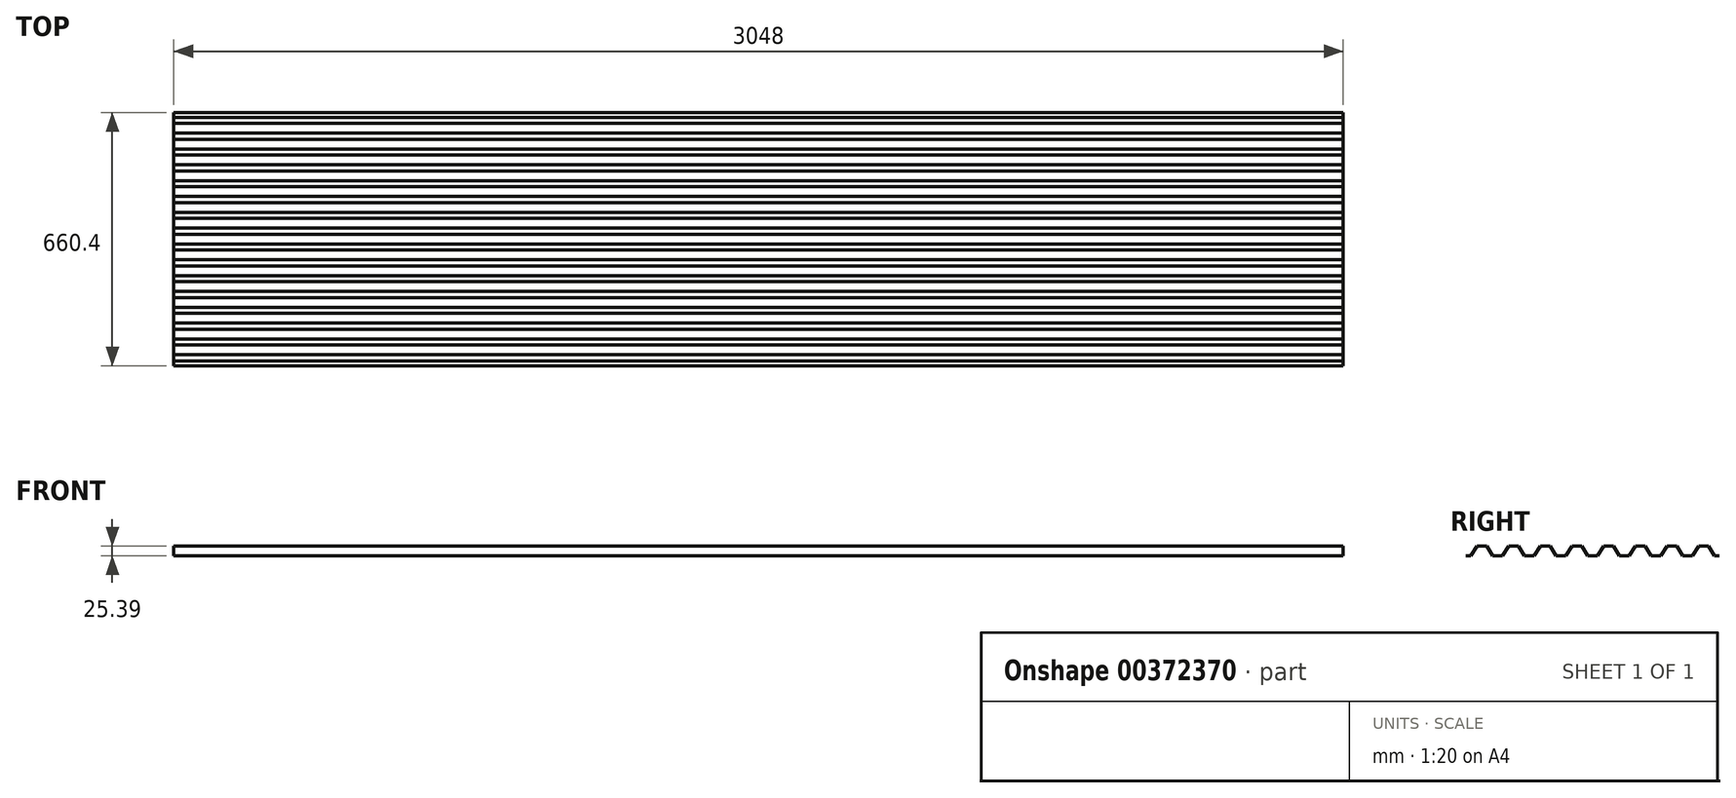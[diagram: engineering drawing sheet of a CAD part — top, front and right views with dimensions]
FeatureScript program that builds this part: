
annotation { "Feature Type Name" : "Feature", "Feature Type Description" : "" }
export const myFeature = defineFeature(function(context is Context, id is Id, definition is map)
    precondition{}
    {
        {
            var Q0;
            Q0=qCreatedBy(makeId("Right.planeOp"),FACE);
            var sketch = newSketch(context, id + "F0", { "sketchPlane" : qUnion([Q0])});
            skLineSegment(sketch, "E0", {"start": v(-328.87, 0) * mm, "end": v(-316.17, 0) * mm});
            skLineSegment(sketch, "E1", {"start": v(-316.17, 0) * mm, "end": v(-300.3, 25.4) * mm});
            skLineSegment(sketch, "E2", {"start": v(-300.3, 25.4) * mm, "end": v(-274.9, 25.4) * mm});
            skLineSegment(sketch, "E3", {"start": v(-274.9, 25.4) * mm, "end": v(-259.02, 0) * mm});
            skLineSegment(sketch, "E4", {"start": v(-259.02, 0) * mm, "end": v(-246.32, 0) * mm});
            skLineSegment(sketch, "E5.1.0.0", {"start": v(-233.62, 0) * mm, "end": v(-217.75, 25.4) * mm});
            skLineSegment(sketch, "E5.1.0.1", {"start": v(-192.35, 25.4) * mm, "end": v(-176.47, 0) * mm});
            skLineSegment(sketch, "E5.1.0.2", {"start": v(-217.75, 25.4) * mm, "end": v(-192.35, 25.4) * mm});
            skLineSegment(sketch, "E5.1.0.3", {"start": v(-246.32, 0) * mm, "end": v(-233.62, 0) * mm});
            skLineSegment(sketch, "E5.1.0.4", {"start": v(-176.47, 0) * mm, "end": v(-163.77, 0) * mm});
            skLineSegment(sketch, "E5.2.0.0", {"start": v(-151.07, 0) * mm, "end": v(-135.2, 25.4) * mm});
            skLineSegment(sketch, "E5.2.0.1", {"start": v(-109.8, 25.4) * mm, "end": v(-93.92, 0) * mm});
            skLineSegment(sketch, "E5.2.0.2", {"start": v(-135.2, 25.4) * mm, "end": v(-109.8, 25.4) * mm});
            skLineSegment(sketch, "E5.2.0.3", {"start": v(-163.77, 0) * mm, "end": v(-151.07, 0) * mm});
            skLineSegment(sketch, "E5.2.0.4", {"start": v(-93.92, 0) * mm, "end": v(-81.22, 0) * mm});
            skLineSegment(sketch, "E5.direction1", {"start": v(-328.87, 0) * mm, "end": v(-246.32, 0) * mm, "construction": true});
            skLineSegment(sketch, "E6.0.3.0", {"start": v(-68.52, 0) * mm, "end": v(-52.65, 25.4) * mm});
            skLineSegment(sketch, "E6.3.3.0", {"start": v(-27.25, 25.4) * mm, "end": v(-11.37, 0) * mm});
            skLineSegment(sketch, "E6.6.3.0", {"start": v(-52.65, 25.4) * mm, "end": v(-27.25, 25.4) * mm});
            skLineSegment(sketch, "E6.9.3.0", {"start": v(-81.22, 0) * mm, "end": v(-68.52, 0) * mm});
            skLineSegment(sketch, "E6.12.3.0", {"start": v(-11.37, 0) * mm, "end": v(1.33, 0) * mm});
            skLineSegment(sketch, "E6.0.4.0", {"start": v(14.03, 0) * mm, "end": v(29.9, 25.4) * mm});
            skLineSegment(sketch, "E6.3.4.0", {"start": v(55.3, 25.4) * mm, "end": v(71.18, 0) * mm});
            skLineSegment(sketch, "E6.6.4.0", {"start": v(29.9, 25.4) * mm, "end": v(55.3, 25.4) * mm});
            skLineSegment(sketch, "E6.9.4.0", {"start": v(1.33, 0) * mm, "end": v(14.03, 0) * mm});
            skLineSegment(sketch, "E6.12.4.0", {"start": v(71.18, 0) * mm, "end": v(83.88, 0) * mm});
            skLineSegment(sketch, "E6.0.5.0", {"start": v(96.58, 0) * mm, "end": v(112.45, 25.4) * mm});
            skLineSegment(sketch, "E6.3.5.0", {"start": v(137.85, 25.4) * mm, "end": v(153.73, 0) * mm});
            skLineSegment(sketch, "E6.6.5.0", {"start": v(112.45, 25.4) * mm, "end": v(137.85, 25.4) * mm});
            skLineSegment(sketch, "E6.9.5.0", {"start": v(83.88, 0) * mm, "end": v(96.58, 0) * mm});
            skLineSegment(sketch, "E6.12.5.0", {"start": v(153.73, 0) * mm, "end": v(166.43, 0) * mm});
            skLineSegment(sketch, "E6.0.6.0", {"start": v(179.13, 0) * mm, "end": v(195, 25.4) * mm});
            skLineSegment(sketch, "E6.3.6.0", {"start": v(220.4, 25.4) * mm, "end": v(236.28, 0) * mm});
            skLineSegment(sketch, "E6.6.6.0", {"start": v(195, 25.4) * mm, "end": v(220.4, 25.4) * mm});
            skLineSegment(sketch, "E6.9.6.0", {"start": v(166.43, 0) * mm, "end": v(179.13, 0) * mm});
            skLineSegment(sketch, "E6.12.6.0", {"start": v(236.28, 0) * mm, "end": v(248.98, 0) * mm});
            skLineSegment(sketch, "E6.0.7.0", {"start": v(261.68, 0) * mm, "end": v(277.55, 25.4) * mm});
            skLineSegment(sketch, "E6.3.7.0", {"start": v(302.95, 25.4) * mm, "end": v(318.83, 0) * mm});
            skLineSegment(sketch, "E6.6.7.0", {"start": v(277.55, 25.4) * mm, "end": v(302.95, 25.4) * mm});
            skLineSegment(sketch, "E6.9.7.0", {"start": v(248.98, 0) * mm, "end": v(261.68, 0) * mm});
            skLineSegment(sketch, "E6.12.7.0", {"start": v(318.83, 0) * mm, "end": v(331.53, 0) * mm});
            skSolve(sketch);
        }
        {
            var Q0;
            Q0=sQuery(id+"F0.wireOp",EDGE,"E6.0.6.0");
            var Q1;
            Q1=sQuery(id+"F0.wireOp",EDGE,"E5.1.0.1");
            var Q2;
            Q2=sQuery(id+"F0.wireOp",EDGE,"E6.6.4.0");
            var Q3;
            Q3=sQuery(id+"F0.wireOp",EDGE,"E6.3.3.0");
            var Q4;
            Q4=sQuery(id+"F0.wireOp",EDGE,"E6.3.5.0");
            var Q5;
            Q5=sQuery(id+"F0.wireOp",EDGE,"E6.3.7.0");
            var Q6;
            Q6=sQuery(id+"F0.wireOp",EDGE,"E3");
            var Q7;
            Q7=sQuery(id+"F0.wireOp",EDGE,"E6.0.7.0");
            var Q8;
            Q8=sQuery(id+"F0.wireOp",EDGE,"E6.6.7.0");
            var Q9;
            Q9=sQuery(id+"F0.wireOp",EDGE,"E5.2.0.0");
            var Q10;
            Q10=sQuery(id+"F0.wireOp",EDGE,"E6.3.4.0");
            var Q11;
            Q11=sQuery(id+"F0.wireOp",EDGE,"E5.1.0.0");
            var Q12;
            Q12=sQuery(id+"F0.wireOp",EDGE,"E6.6.3.0");
            var Q13;
            Q13=sQuery(id+"F0.wireOp",EDGE,"E1");
            var Q14;
            Q14=sQuery(id+"F0.wireOp",EDGE,"E2");
            var Q15;
            Q15=sQuery(id+"F0.wireOp",EDGE,"E6.0.3.0");
            var Q16;
            Q16=sQuery(id+"F0.wireOp",EDGE,"E5.1.0.2");
            var Q17;
            Q17=sQuery(id+"F0.wireOp",EDGE,"E6.6.6.0");
            var Q18;
            Q18=sQuery(id+"F0.wireOp",EDGE,"E6.0.5.0");
            var Q19;
            Q19=sQuery(id+"F0.wireOp",EDGE,"E6.3.6.0");
            var Q20;
            Q20=sQuery(id+"F0.wireOp",EDGE,"E6.6.5.0");
            var Q21;
            Q21=sQuery(id+"F0.wireOp",EDGE,"E5.2.0.2");
            var Q22;
            Q22=sQuery(id+"F0.wireOp",EDGE,"E6.0.4.0");
            var Q23;
            Q23=sQuery(id+"F0.wireOp",EDGE,"E5.2.0.1");
            var Q24;
            Q24=sQuery(id+"F0.wireOp",EDGE,"E6.12.7.0");
            var Q25;
            Q25=sQuery(id+"F0.wireOp",EDGE,"E6.12.4.0");
            var Q26;
            Q26=sQuery(id+"F0.wireOp",EDGE,"E4");
            var Q27;
            Q27=sQuery(id+"F0.wireOp",EDGE,"E6.12.3.0");
            var Q28;
            Q28=sQuery(id+"F0.wireOp",EDGE,"E6.9.3.0");
            var Q29;
            Q29=sQuery(id+"F0.wireOp",EDGE,"E5.2.0.3");
            var Q30;
            Q30=sQuery(id+"F0.wireOp",EDGE,"E6.9.4.0");
            var Q31;
            Q31=sQuery(id+"F0.wireOp",EDGE,"E5.2.0.4");
            var Q32;
            Q32=sQuery(id+"F0.wireOp",EDGE,"E6.9.5.0");
            var Q33;
            Q33=sQuery(id+"F0.wireOp",EDGE,"E6.9.7.0");
            var Q34;
            Q34=sQuery(id+"F0.wireOp",EDGE,"E6.12.6.0");
            var Q35;
            Q35=sQuery(id+"F0.wireOp",EDGE,"E6.12.5.0");
            var Q36;
            Q36=sQuery(id+"F0.wireOp",EDGE,"E5.1.0.4");
            var Q37;
            Q37=sQuery(id+"F0.wireOp",EDGE,"E5.1.0.3");
            var Q38;
            Q38=sQuery(id+"F0.wireOp",EDGE,"E0");
            var Q39;
            Q39=sQuery(id+"F0.wireOp",EDGE,"E6.9.6.0");
            extrude(context, id + "F1", {"bodyType" : ToolBodyType.SURFACE, "surfaceEntities" : qUnion([Q0, Q1, Q2, Q3, Q4, Q5, Q6, Q7, Q8, Q9, Q10, Q11, Q12, Q13, Q14, Q15, Q16, Q17, Q18, Q19, Q20, Q21, Q22, Q23, Q24, Q25, Q26, Q27, Q28, Q29, Q30, Q31, Q32, Q33, Q34, Q35, Q36, Q37, Q38, Q39]), "endBound" : BoundingType.SYMMETRIC, "depth" : 3048 * mm});
        }
    });
